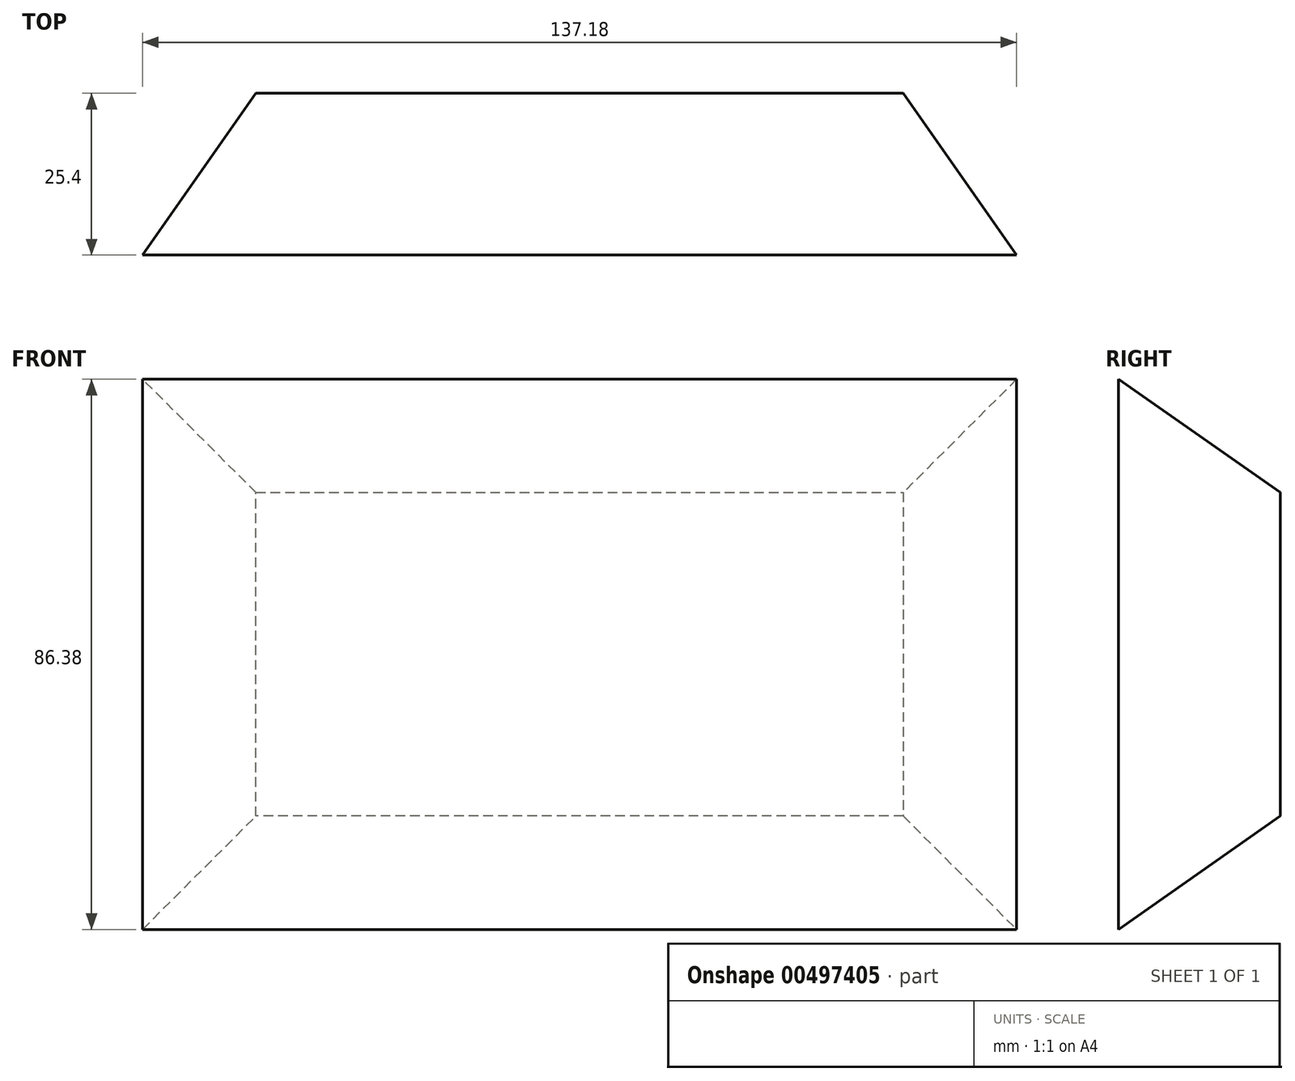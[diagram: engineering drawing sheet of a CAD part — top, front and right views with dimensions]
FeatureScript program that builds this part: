
annotation { "Feature Type Name" : "Feature", "Feature Type Description" : "" }
export const myFeature = defineFeature(function(context is Context, id is Id, definition is map)
    precondition{}
    {
        {
            var Q0;
            Q0=qCreatedBy(makeId("Front.planeOp"),FACE);
            var sketch = newSketch(context, id + "F0", { "sketchPlane" : qUnion([Q0])});
            skLineSegment(sketch, "E0.bottom", {"start": v(50.8, -25.4) * mm, "end": v(-50.8, -25.4) * mm});
            skLineSegment(sketch, "E0.top", {"start": v(50.8, 25.4) * mm, "end": v(-50.8, 25.4) * mm});
            skLineSegment(sketch, "E0.left", {"start": v(50.8, -25.4) * mm, "end": v(50.8, 25.4) * mm});
            skLineSegment(sketch, "E0.right", {"start": v(-50.8, -25.4) * mm, "end": v(-50.8, 25.4) * mm});
            skPoint(sketch, "E0.middle", {"position": v(0, 0) * mm});
            skSolve(sketch);
        }
        {
            var Q0;
            Q0 = qSketchRegion(id + "F0", true);
            extrude(context, id + "F1", {"entities" : qUnion([Q0]), "depth" : 25.4 * mm, "hasDraft" : true, "draftAngle" : 35 * degree});
        }
    });
